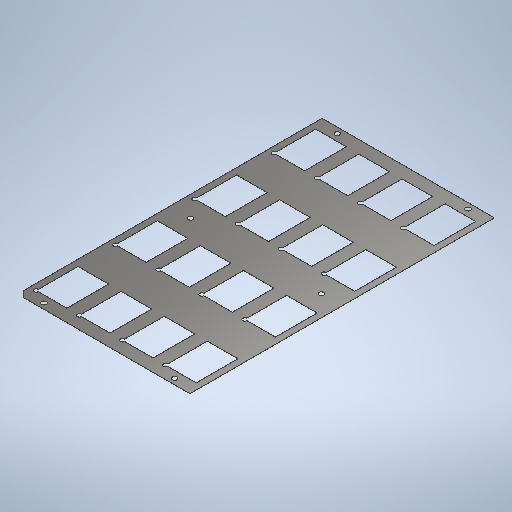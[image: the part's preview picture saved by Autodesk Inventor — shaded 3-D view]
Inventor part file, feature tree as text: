
AUTODESK INVENTOR PART (.ipt)
format: ipt  version: 2025 (Build 290162000, 162)  size: 418,816 bytes
history: native  units: in
note: dims shown in document units (in); Inventor stores cm internally (conversion verified against a paired STEP export)
features: extrude x2, sketch x2, chamfer x1, fillet x1, hole x1
ambient origin geometry x8: Origin, YZ Plane, XZ Plane, XY Plane, X Axis, Y Axis, Z Axis, Center Point
bodies: Solid1 (feature_tree)
feature tree (7):
  extrude  "Extrusion1"  Depth=4.8819in
  chamfer  "Chamfer1"  Distance=0.0039in
  extrude  "Extrusion2"  Depth=0.0394in TaperAngle=45.0deg
  fillet  "Fillet1"  Radius=0.0591in
  hole  "Hole1"  [1 undecoded]
  sketch  "Sketch Rectangular Pattern1"  dims[d0=8.622in d1=4.8819in d2=0.0039in d3=0.0in]
  sketch  "Sketch3"  dims[d18=0.0in d19=0.0in d38=0.1575in d39=0.125in d40=45.0deg d46=0.0591in d47=1.1811in d50=0.3543in d51=0.1772in d60=1.5748in d62=2.2441in d63=1.5748in d65=1.2205in d77=0.8661in d89=0.0394in d90=0.5906in d91=0.5906in d92=0.1575in d93=0.1575in d94=0.1339in d95=0.2362in d96=0.248in d97=0.0787in d98=90.0deg d99=0.3465in d100=0.8108in]
note: 1 required parameter value undecoded (feature->parameter linkage not recoverable at this tier; creation-order binding heuristic only, values carry confidence <= 0.55)
